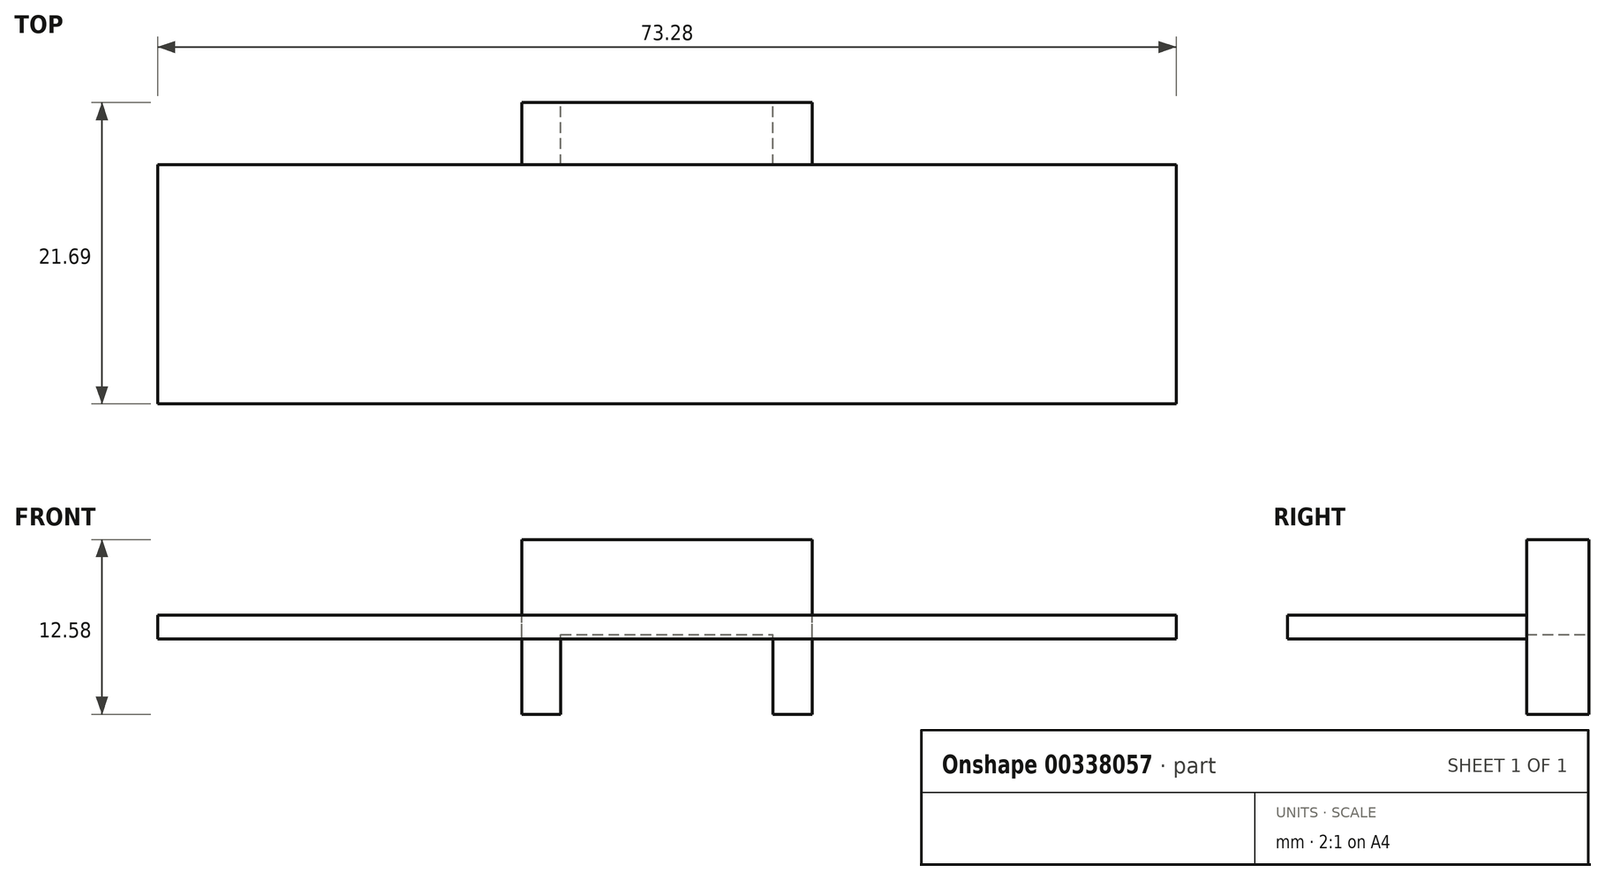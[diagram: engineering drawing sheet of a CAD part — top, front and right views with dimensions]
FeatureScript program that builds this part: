
annotation { "Feature Type Name" : "Feature", "Feature Type Description" : "" }
export const myFeature = defineFeature(function(context is Context, id is Id, definition is map)
    precondition{}
    {
        {
            var Q0;
            Q0=qCreatedBy(makeId("Top.planeOp"),FACE);
            var sketch = newSketch(context, id + "F0", { "sketchPlane" : qUnion([Q0])});
            skLineSegment(sketch, "E0.bottom", {"start": v(36.65, -8.6) * mm, "end": v(-36.65, -8.6) * mm});
            skLineSegment(sketch, "E0.top", {"start": v(36.65, 8.6) * mm, "end": v(-36.65, 8.6) * mm});
            skLineSegment(sketch, "E0.left", {"start": v(36.65, -8.6) * mm, "end": v(36.65, 8.6) * mm});
            skLineSegment(sketch, "E0.right", {"start": v(-36.65, -8.6) * mm, "end": v(-36.65, 8.6) * mm});
            skPoint(sketch, "E0.middle", {"position": v(0, 0) * mm});
            skSolve(sketch);
        }
        {
            var Q0;
            Q0=qSketchRegion(id+"F0",true);
            extrude(context, id + "F1", {"entities" : qUnion([Q0]), "endBound" : BoundingType.SYMMETRIC, "depth" : 1.71 * mm});
        }
        {
            var Q0;
            Q0=qCreatedBy(makeId("Right.planeOp"),FACE);
            var sketch = newSketch(context, id + "F2", { "sketchPlane" : qUnion([Q0])});
            skLineSegment(sketch, "E1.bottom", {"start": v(13.08, -6.29) * mm, "end": v(8.6, -6.29) * mm});
            skLineSegment(sketch, "E1.top", {"start": v(13.08, 6.29) * mm, "end": v(8.6, 6.29) * mm});
            skLineSegment(sketch, "E1.left", {"start": v(13.08, -6.29) * mm, "end": v(13.08, 6.29) * mm});
            skLineSegment(sketch, "E1.right", {"start": v(8.6, -6.29) * mm, "end": v(8.6, 6.29) * mm});
            skPoint(sketch, "E1.middle", {"position": v(10.84, 0) * mm});
            skSolve(sketch);
        }
        {
            var Q0;
            Q0=qSketchRegion(id+"F2",true);
            extrude(context, id + "F3", {"entities" : qUnion([Q0]), "endBound" : BoundingType.SYMMETRIC, "depth" : 20.9 * mm});
        }
        {
            var Q0;
            Q0=makeQuery(id+"F3.opExtrude","SWEPT_FACE",FACE,{"disambiguationData":[OSD([sQuery(id+"F2.wireOp",EDGE,"E1.left")])]});
            var sketch = newSketch(context, id + "F4", { "sketchPlane" : qUnion([Q0])});
            skLineSegment(sketch, "E2.bottom", {"start": v(7.64, -6.29) * mm, "end": v(-7.64, -6.29) * mm});
            skLineSegment(sketch, "E2.top", {"start": v(7.64, -0.57) * mm, "end": v(-7.64, -0.57) * mm});
            skLineSegment(sketch, "E2.left", {"start": v(7.64, -6.29) * mm, "end": v(7.64, -0.57) * mm});
            skLineSegment(sketch, "E2.right", {"start": v(-7.64, -6.29) * mm, "end": v(-7.64, -0.57) * mm});
            skPoint(sketch, "E2.middle", {"position": v(0, -3.43) * mm});
            skSolve(sketch);
        }
        {
            var Q0;
            Q0=qSketchRegion(id+"F4",true);
            var Q1;
            {var subQ0=sQuery(id+"F2.wireOp",EDGE,"E1.right");var subQ3=sQuery(id+"F2.wireOp",EDGE,"E1.bottom");Q1=makeQuery(id+"F3.boolean.opBoolean","SPLIT",FACE,{"disambiguationData":[TD([makeQuery(id+"F3.opExtrude","SWEPT_FACE",FACE,{"disambiguationData":[OSD([subQ3])]})])],"derivedFrom":makeQuery(id+"F3.opExtrude","SWEPT_FACE",FACE,{"disambiguationData":[OSD([subQ0])]})});}
            extrude(context, id + "F5", {"entities" : qUnion([Q0]), "operationType" : NewBodyOperationType.REMOVE, "endBound" : BoundingType.UP_TO_SURFACE, "oppositeDirection" : true, "endBoundEntityFace" : qUnion([Q1]), "depth" : 25 * mm});
        }
    });
